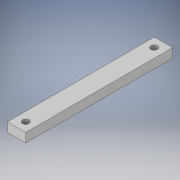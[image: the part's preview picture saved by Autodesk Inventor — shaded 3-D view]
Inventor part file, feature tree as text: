
AUTODESK INVENTOR PART (.ipt)
format: ipt  version: 2019 (Build 230136000, 136)  size: 107,520 bytes
history: native  units: in
note: dims shown in document units (in); Inventor stores cm internally (conversion verified against a paired STEP export)
features: sketch x2, extrude x1, hole x1, projected_geometry x1
ambient origin geometry x8: Origin, YZ Plane, XZ Plane, XY Plane, X Axis, Y Axis, Z Axis, Center Point
bodies: Solid1 (feature_tree)
feature tree (5):
  extrude  "Extrusion1"  Depth=8.0in
  hole  "Hole1"  [1 undecoded]
  sketch  "Sketch1"  dims[d0=1.0in d1=8.0in]
  sketch  "Sketch2"  dims[d2=0.5in d3=0.0in d4=8.0in d5=1.0in d6=0.5in d7=0.5in d8=7.0in d9=0.5in d10=0.35in d11=0.75in d12=0.375in d13=0.25in d14=0.5635in d15=1.0in d16=0.8108in]
  projected_geometry  "Projected Loop1"
note: 1 required parameter value undecoded (feature->parameter linkage not recoverable at this tier; creation-order binding heuristic only, values carry confidence <= 0.55)
